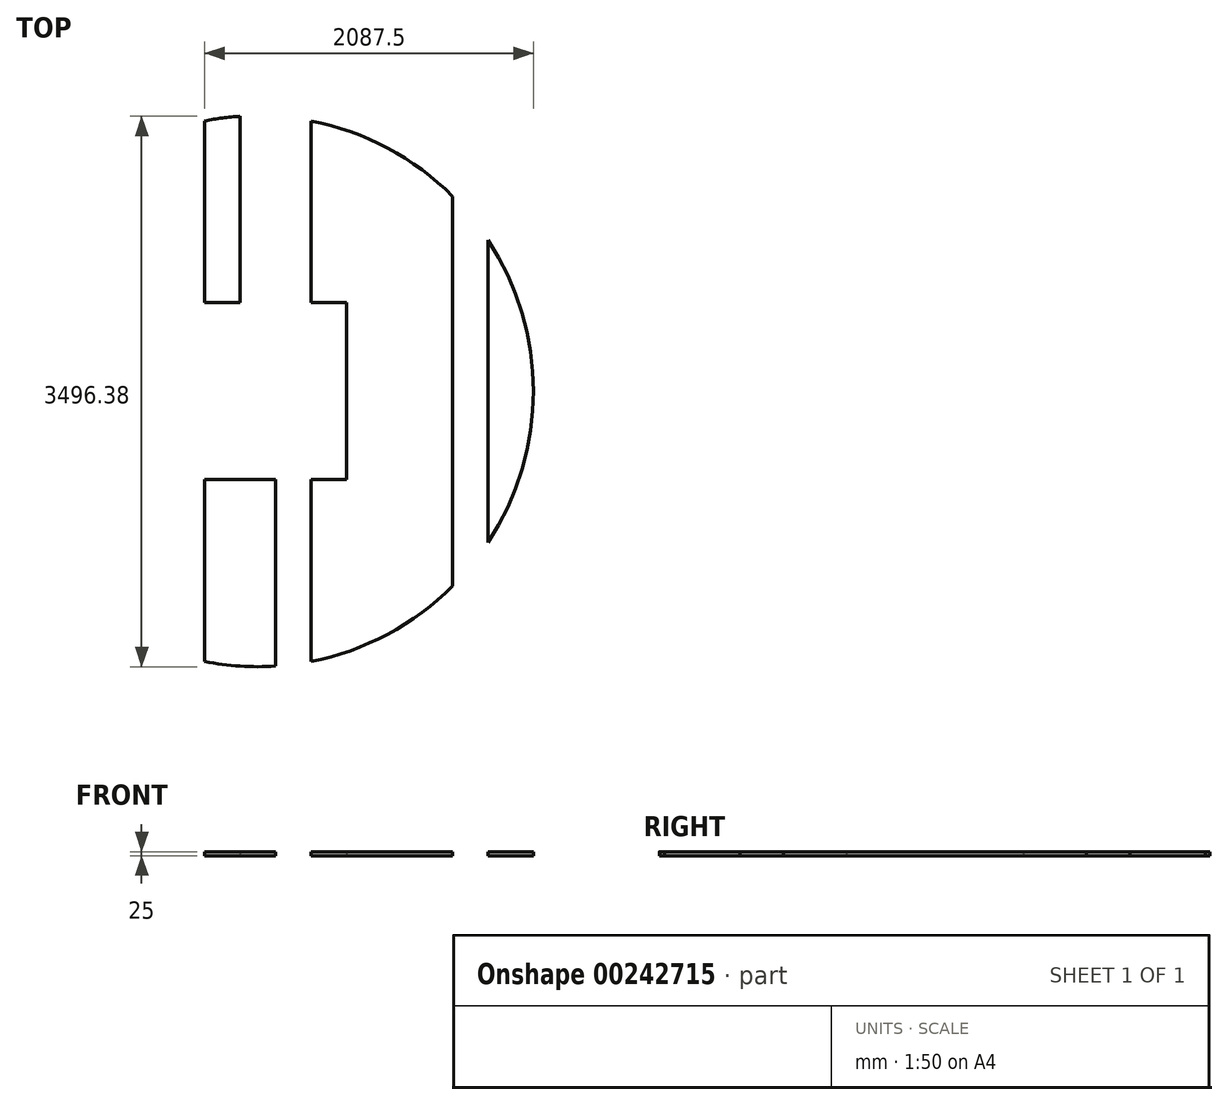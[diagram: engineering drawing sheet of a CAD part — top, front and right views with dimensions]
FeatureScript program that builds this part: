
annotation { "Feature Type Name" : "Feature", "Feature Type Description" : "" }
export const myFeature = defineFeature(function(context is Context, id is Id, definition is map)
    precondition{}
    {
        {
            var Q0;
            Q0=qCreatedBy(makeId("Top.planeOp"),FACE);
            var sketch = newSketch(context, id + "F0", { "sketchPlane" : qUnion([Q0])});
            skLineSegment(sketch, "E0.bottom", {"start": v(-450, 3679.72) * mm, "end": v(-225, 3679.72) * mm});
            skLineSegment(sketch, "E0.top", {"start": v(-450, -320.28) * mm, "end": v(-225, -320.28) * mm});
            skLineSegment(sketch, "E0.left", {"start": v(-450, 3679.72) * mm, "end": v(-450, -320.28) * mm});
            skLineSegment(sketch, "E0.right", {"start": v(-225, 3679.72) * mm, "end": v(-225, -320.28) * mm});
            skPoint(sketch, "E1.centerSnap0", {"position": v(-225, 1679.72) * mm});
            skCircle(sketch, "E2", {"center": v(-562.5, 1679.72) * mm, "radius": 1750 * mm});
            skLineSegment(sketch, "E3.bottom", {"start": v(-450, 3679.72) * mm, "end": v(-675, 3679.72) * mm});
            skLineSegment(sketch, "E3.top", {"start": v(-450, -320.28) * mm, "end": v(-675, -320.28) * mm});
            skLineSegment(sketch, "E3.right", {"start": v(-675, 3679.72) * mm, "end": v(-675, -320.28) * mm});
            skLineSegment(sketch, "E4.bottom", {"start": v(-900, 3679.72) * mm, "end": v(-675, 3679.72) * mm});
            skLineSegment(sketch, "E4.top", {"start": v(-900, -320.28) * mm, "end": v(-675, -320.28) * mm});
            skLineSegment(sketch, "E4.left", {"start": v(-900, 3679.72) * mm, "end": v(-900, -320.28) * mm});
            skLineSegment(sketch, "E5.bottom", {"start": v(-1714.35, 3645.18) * mm, "end": v(-1493.78, 3645.18) * mm});
            skLineSegment(sketch, "E5.top", {"start": v(-1714.35, 3499.85) * mm, "end": v(-1493.78, 3499.85) * mm});
            skLineSegment(sketch, "E5.left", {"start": v(-1714.35, 3645.18) * mm, "end": v(-1714.35, 3499.85) * mm});
            skLineSegment(sketch, "E5.right", {"start": v(-1493.78, 3645.18) * mm, "end": v(-1493.78, 3499.85) * mm});
            skLineSegment(sketch, "E6.bottom", {"start": v(-225, 3679.72) * mm, "end": v(0, 3679.72) * mm});
            skLineSegment(sketch, "E6.top", {"start": v(-225, -320.28) * mm, "end": v(0, -320.28) * mm});
            skLineSegment(sketch, "E6.right", {"start": v(0, 3679.72) * mm, "end": v(0, -320.28) * mm});
            skLineSegment(sketch, "E7.bottom", {"start": v(0, 3679.72) * mm, "end": v(225, 3679.72) * mm});
            skLineSegment(sketch, "E7.top", {"start": v(0, -320.28) * mm, "end": v(225, -320.28) * mm});
            skLineSegment(sketch, "E7.right", {"start": v(225, 3679.72) * mm, "end": v(225, -320.28) * mm});
            skLineSegment(sketch, "E8.bottom", {"start": v(225, 3679.72) * mm, "end": v(450, 3679.72) * mm});
            skLineSegment(sketch, "E8.top", {"start": v(225, -320.28) * mm, "end": v(450, -320.28) * mm});
            skLineSegment(sketch, "E8.right", {"start": v(450, 3679.72) * mm, "end": v(450, -320.28) * mm});
            skLineSegment(sketch, "E9.bottom", {"start": v(450, 3679.72) * mm, "end": v(675, 3679.72) * mm});
            skLineSegment(sketch, "E9.top", {"start": v(450, -320.28) * mm, "end": v(675, -320.28) * mm});
            skLineSegment(sketch, "E9.right", {"start": v(675, 3679.72) * mm, "end": v(675, -320.28) * mm});
            skLineSegment(sketch, "E10.bottom", {"start": v(675, 3679.72) * mm, "end": v(900, 3679.72) * mm});
            skLineSegment(sketch, "E10.top", {"start": v(675, -320.28) * mm, "end": v(900, -320.28) * mm});
            skLineSegment(sketch, "E10.right", {"start": v(900, 3679.72) * mm, "end": v(900, -320.28) * mm});
            skLineSegment(sketch, "E11.bottom", {"start": v(900, 3679.72) * mm, "end": v(1125, 3679.72) * mm});
            skLineSegment(sketch, "E11.top", {"start": v(900, -320.28) * mm, "end": v(1125, -320.28) * mm});
            skLineSegment(sketch, "E11.right", {"start": v(1125, 3679.72) * mm, "end": v(1125, -320.28) * mm});
            skLineSegment(sketch, "E12.bottom", {"start": v(-1124.5, 2241.72) * mm, "end": v(-0.5, 2241.72) * mm});
            skLineSegment(sketch, "E12.top", {"start": v(-1124.5, 1117.72) * mm, "end": v(-0.5, 1117.72) * mm});
            skLineSegment(sketch, "E12.left", {"start": v(-1124.5, 2241.72) * mm, "end": v(-1124.5, 1117.72) * mm});
            skLineSegment(sketch, "E12.right", {"start": v(-0.5, 2241.72) * mm, "end": v(-0.5, 1117.72) * mm});
            skSolve(sketch);
        }
        {
            var Q0;
            {var subQ0=sQuery(id+"F0.wireOp",EDGE,"E4.left");var subQ1=sQuery(id+"F0.wireOp",EDGE,"E2");var subQ2=makeQuery(id+"F0.imprint","INTERSECT",VERTEX,{"disambiguationData":[OD(0.0)],"derivedFrom":[subQ1,subQ0]});Q0=makeQuery(id+"F0.imprint","IMPRINT",FACE,{"disambiguationData":[TD([[makeQuery(id+"F0.imprint","IMPRINT",EDGE,{"disambiguationData":[TD([[subQ2,1.0]])],"derivedFrom":subQ1}),1.0]])]});}
            var Q1;
            {var subQ0=sQuery(id+"F0.wireOp",EDGE,"E0.left");var subQ1=sQuery(id+"F0.wireOp",EDGE,"E2");var subQ2=makeQuery(id+"F0.imprint","INTERSECT",VERTEX,{"disambiguationData":[OD(0.0)],"derivedFrom":[subQ1,subQ0]});Q1=makeQuery(id+"F0.imprint","IMPRINT",FACE,{"disambiguationData":[TD([[makeQuery(id+"F0.imprint","IMPRINT",EDGE,{"disambiguationData":[TD([[subQ2,-1.0]])],"derivedFrom":subQ1}),1.0]])]});}
            var Q2;
            {var subQ0=sQuery(id+"F0.wireOp",EDGE,"E4.left");var subQ1=sQuery(id+"F0.wireOp",EDGE,"E2");var subQ2=makeQuery(id+"F0.imprint","INTERSECT",VERTEX,{"disambiguationData":[OD(1.0)],"derivedFrom":[subQ1,subQ0]});Q2=makeQuery(id+"F0.imprint","IMPRINT",FACE,{"disambiguationData":[TD([[makeQuery(id+"F0.imprint","IMPRINT",EDGE,{"disambiguationData":[TD([[subQ2,-1.0]])],"derivedFrom":subQ1}),1.0]])]});}
            var Q3;
            {var subQ0=sQuery(id+"F0.wireOp",EDGE,"E3.right");var subQ1=sQuery(id+"F0.wireOp",EDGE,"E2");var subQ2=makeQuery(id+"F0.imprint","INTERSECT",VERTEX,{"disambiguationData":[OD(1.0)],"derivedFrom":[subQ1,subQ0]});Q3=makeQuery(id+"F0.imprint","IMPRINT",FACE,{"disambiguationData":[TD([[makeQuery(id+"F0.imprint","IMPRINT",EDGE,{"disambiguationData":[TD([[subQ2,-1.0]])],"derivedFrom":subQ1}),1.0]])]});}
            var Q4;
            {var subQ0=sQuery(id+"F0.wireOp",EDGE,"E0.left");var subQ1=sQuery(id+"F0.wireOp",EDGE,"E2");var subQ2=makeQuery(id+"F0.imprint","INTERSECT",VERTEX,{"disambiguationData":[OD(1.0)],"derivedFrom":[subQ1,subQ0]});Q4=makeQuery(id+"F0.imprint","IMPRINT",FACE,{"disambiguationData":[TD([[makeQuery(id+"F0.imprint","IMPRINT",EDGE,{"disambiguationData":[TD([[subQ2,-1.0]])],"derivedFrom":subQ1}),1.0]])]});}
            var Q5;
            {var subQ0=sQuery(id+"F0.wireOp",EDGE,"E0.right");var subQ1=sQuery(id+"F0.wireOp",EDGE,"E2");var subQ2=makeQuery(id+"F0.imprint","INTERSECT",VERTEX,{"disambiguationData":[OD(1.0)],"derivedFrom":[subQ1,subQ0]});Q5=makeQuery(id+"F0.imprint","IMPRINT",FACE,{"disambiguationData":[TD([[makeQuery(id+"F0.imprint","IMPRINT",EDGE,{"disambiguationData":[TD([[subQ2,-1.0]])],"derivedFrom":subQ1}),1.0]])]});}
            var Q6;
            {var subQ5=sQuery(id+"F0.wireOp",EDGE,"E12.right");Q6=makeQuery(id+"F0.imprint","IMPRINT",FACE,{"disambiguationData":[TD([[makeQuery(id+"F0.imprint","IMPRINT",EDGE,{"derivedFrom":subQ5}),1.0]])]});}
            var Q7;
            {var subQ0=sQuery(id+"F0.wireOp",EDGE,"E8.right");var subQ1=sQuery(id+"F0.wireOp",EDGE,"E2");var subQ2=makeQuery(id+"F0.imprint","INTERSECT",VERTEX,{"disambiguationData":[OD(0.0)],"derivedFrom":[subQ1,subQ0]});Q7=makeQuery(id+"F0.imprint","IMPRINT",FACE,{"disambiguationData":[TD([[makeQuery(id+"F0.imprint","IMPRINT",EDGE,{"disambiguationData":[TD([[subQ2,-1.0]])],"derivedFrom":subQ1}),1.0]])]});}
            var Q8;
            {var subQ0=sQuery(id+"F0.wireOp",EDGE,"E10.right");var subQ1=sQuery(id+"F0.wireOp",EDGE,"E2");var subQ2=makeQuery(id+"F0.imprint","INTERSECT",VERTEX,{"disambiguationData":[OD(0.0)],"derivedFrom":[subQ1,subQ0]});Q8=makeQuery(id+"F0.imprint","IMPRINT",FACE,{"disambiguationData":[TD([[makeQuery(id+"F0.imprint","IMPRINT",EDGE,{"disambiguationData":[TD([[subQ2,-1.0]])],"derivedFrom":subQ1}),1.0]])]});}
            var Q9;
            {var subQ0=sQuery(id+"F0.wireOp",EDGE,"E11.right");var subQ1=sQuery(id+"F0.wireOp",EDGE,"E2");var subQ2=makeQuery(id+"F0.imprint","INTERSECT",VERTEX,{"disambiguationData":[OD(0.0)],"derivedFrom":[subQ1,subQ0]});Q9=makeQuery(id+"F0.imprint","IMPRINT",FACE,{"disambiguationData":[TD([[makeQuery(id+"F0.imprint","IMPRINT",EDGE,{"disambiguationData":[TD([[subQ2,-1.0]])],"derivedFrom":subQ1}),1.0]])]});}
            var Q10;
            {var subQ0=sQuery(id+"F0.wireOp",EDGE,"E11.right");var subQ1=sQuery(id+"F0.wireOp",EDGE,"E2");var subQ2=makeQuery(id+"F0.imprint","INTERSECT",VERTEX,{"disambiguationData":[OD(0.0)],"derivedFrom":[subQ1,subQ0]});Q10=makeQuery(id+"F0.imprint","IMPRINT",FACE,{"disambiguationData":[TD([[makeQuery(id+"F0.imprint","IMPRINT",EDGE,{"disambiguationData":[TD([[subQ2,1.0]])],"derivedFrom":subQ1}),1.0]])]});}
            var Q11;
            {var subQ0=sQuery(id+"F0.wireOp",EDGE,"E9.right");var subQ1=sQuery(id+"F0.wireOp",EDGE,"E2");var subQ2=makeQuery(id+"F0.imprint","INTERSECT",VERTEX,{"disambiguationData":[OD(0.0)],"derivedFrom":[subQ1,subQ0]});Q11=makeQuery(id+"F0.imprint","IMPRINT",FACE,{"disambiguationData":[TD([[makeQuery(id+"F0.imprint","IMPRINT",EDGE,{"disambiguationData":[TD([[subQ2,-1.0]])],"derivedFrom":subQ1}),1.0]])]});}
            var Q12;
            {var subQ0=sQuery(id+"F0.wireOp",EDGE,"E6.right");var subQ1=sQuery(id+"F0.wireOp",EDGE,"E2");var subQ2=makeQuery(id+"F0.imprint","INTERSECT",VERTEX,{"disambiguationData":[OD(0.0)],"derivedFrom":[subQ1,subQ0]});Q12=makeQuery(id+"F0.imprint","IMPRINT",FACE,{"disambiguationData":[TD([[makeQuery(id+"F0.imprint","IMPRINT",EDGE,{"disambiguationData":[TD([[subQ2,-1.0]])],"derivedFrom":subQ1}),1.0]])]});}
            var Q13;
            {var subQ0=sQuery(id+"F0.wireOp",EDGE,"E0.right");var subQ1=sQuery(id+"F0.wireOp",EDGE,"E2");var subQ2=makeQuery(id+"F0.imprint","INTERSECT",VERTEX,{"disambiguationData":[OD(0.0)],"derivedFrom":[subQ1,subQ0]});Q13=makeQuery(id+"F0.imprint","IMPRINT",FACE,{"disambiguationData":[TD([[makeQuery(id+"F0.imprint","IMPRINT",EDGE,{"disambiguationData":[TD([[subQ2,-1.0]])],"derivedFrom":subQ1}),1.0]])]});}
            var Q14;
            {var subQ0=sQuery(id+"F0.wireOp",EDGE,"E7.right");var subQ1=sQuery(id+"F0.wireOp",EDGE,"E2");var subQ2=makeQuery(id+"F0.imprint","INTERSECT",VERTEX,{"disambiguationData":[OD(0.0)],"derivedFrom":[subQ1,subQ0]});Q14=makeQuery(id+"F0.imprint","IMPRINT",FACE,{"disambiguationData":[TD([[makeQuery(id+"F0.imprint","IMPRINT",EDGE,{"disambiguationData":[TD([[subQ2,-1.0]])],"derivedFrom":subQ1}),1.0]])]});}
            extrude(context, id + "F1", {"entities" : qUnion([Q0, Q1, Q2, Q3, Q4, Q5, Q6, Q7, Q8, Q9, Q10, Q11, Q12, Q13, Q14]), "depth" : 25 * mm});
        }
    });
